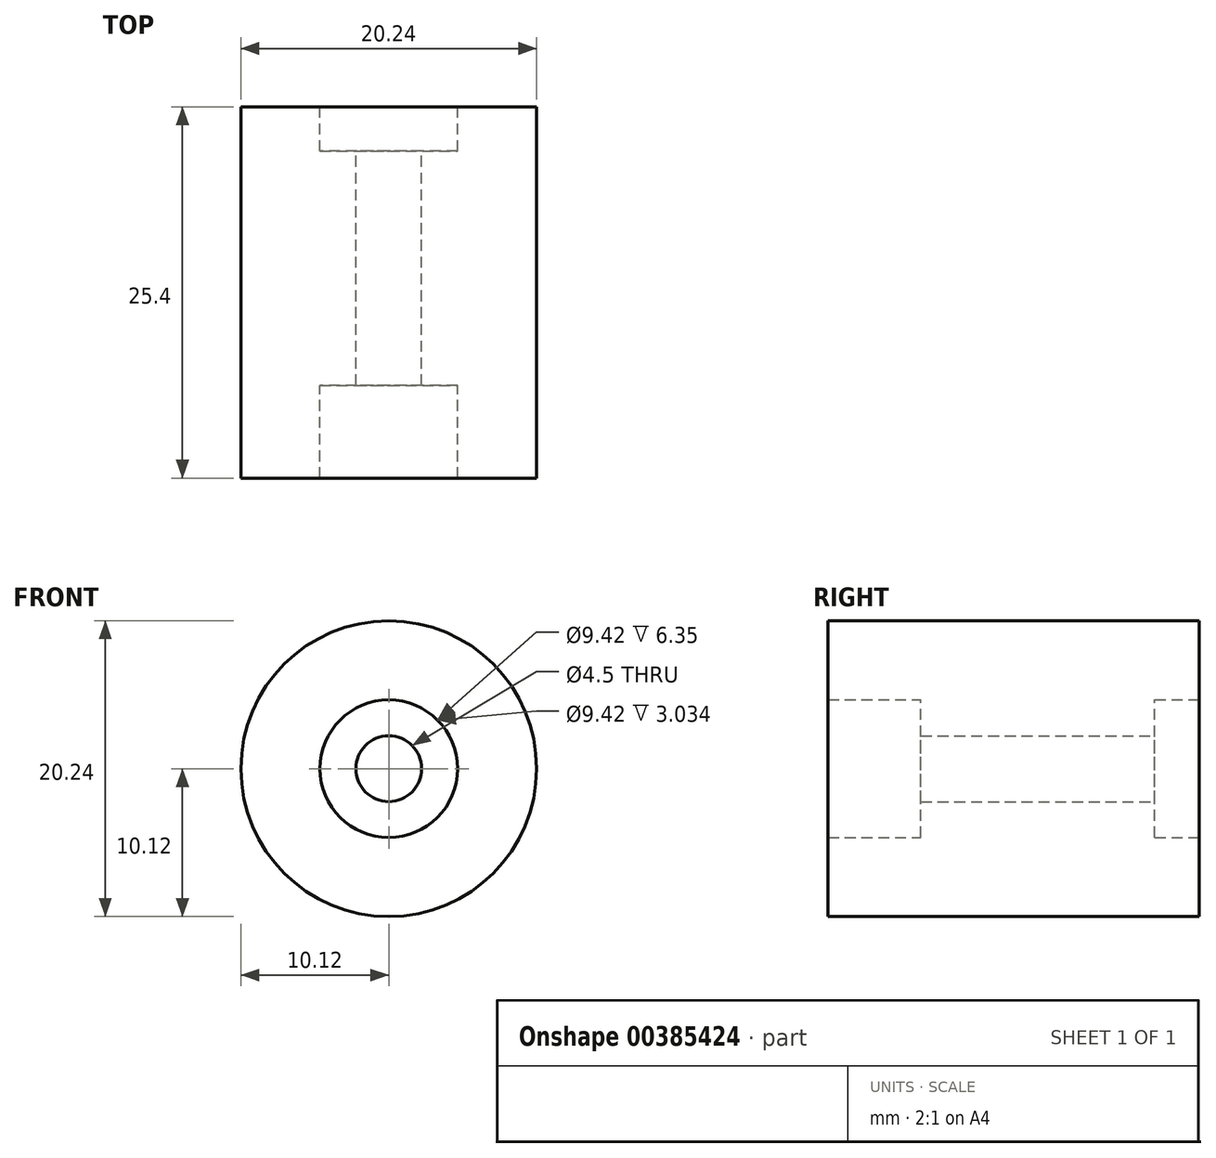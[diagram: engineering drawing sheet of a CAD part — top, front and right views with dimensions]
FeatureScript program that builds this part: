
annotation { "Feature Type Name" : "Feature", "Feature Type Description" : "" }
export const myFeature = defineFeature(function(context is Context, id is Id, definition is map)
    precondition{}
    {
        {
            var Q0;
            Q0=qCreatedBy(makeId("Front.planeOp"),FACE);
            var sketch = newSketch(context, id + "F0", { "sketchPlane" : qUnion([Q0])});
            skCircle(sketch, "E0", {"center": v(0, 0) * mm, "radius": 10.12 * mm});
            skCircle(sketch, "E1", {"center": v(0, 0) * mm, "radius": 4.7 * mm});
            skCircle(sketch, "E2", {"center": v(0, 0) * mm, "radius": 2.25 * mm});
            skSolve(sketch);
        }
        {
            var Q0;
            Q0=makeQuery(id+"F0.imprint","IMPRINT",FACE,{"disambiguationData":[TD([[makeQuery(id+"F0.imprint","IMPRINT",EDGE,{"derivedFrom":sQuery(id+"F0.wireOp",EDGE,"E0")}),1.0]])]});
            extrude(context, id + "F1", {"entities" : qUnion([Q0]), "depth" : 25.4 * mm});
        }
        {
            var Q0;
            Q0=makeQuery(id+"F0.imprint","IMPRINT",FACE,{"disambiguationData":[TD([[makeQuery(id+"F0.imprint","IMPRINT",EDGE,{"derivedFrom":sQuery(id+"F0.wireOp",EDGE,"E1")}),1.0]])]});
            extrude(context, id + "F2", {"entities" : qUnion([Q0]), "operationType" : NewBodyOperationType.ADD, "depth" : 19.05 * mm});
        }
        {
            var Q0;
            Q0=makeQuery(id+"F0.imprint","IMPRINT",FACE,{"disambiguationData":[TD([[makeQuery(id+"F0.imprint","IMPRINT",EDGE,{"derivedFrom":sQuery(id+"F0.wireOp",EDGE,"E1")}),1.0]])]});
            extrude(context, id + "F3", {"entities" : qUnion([Q0]), "operationType" : NewBodyOperationType.REMOVE, "depth" : 3.03 * mm});
        }
    });
